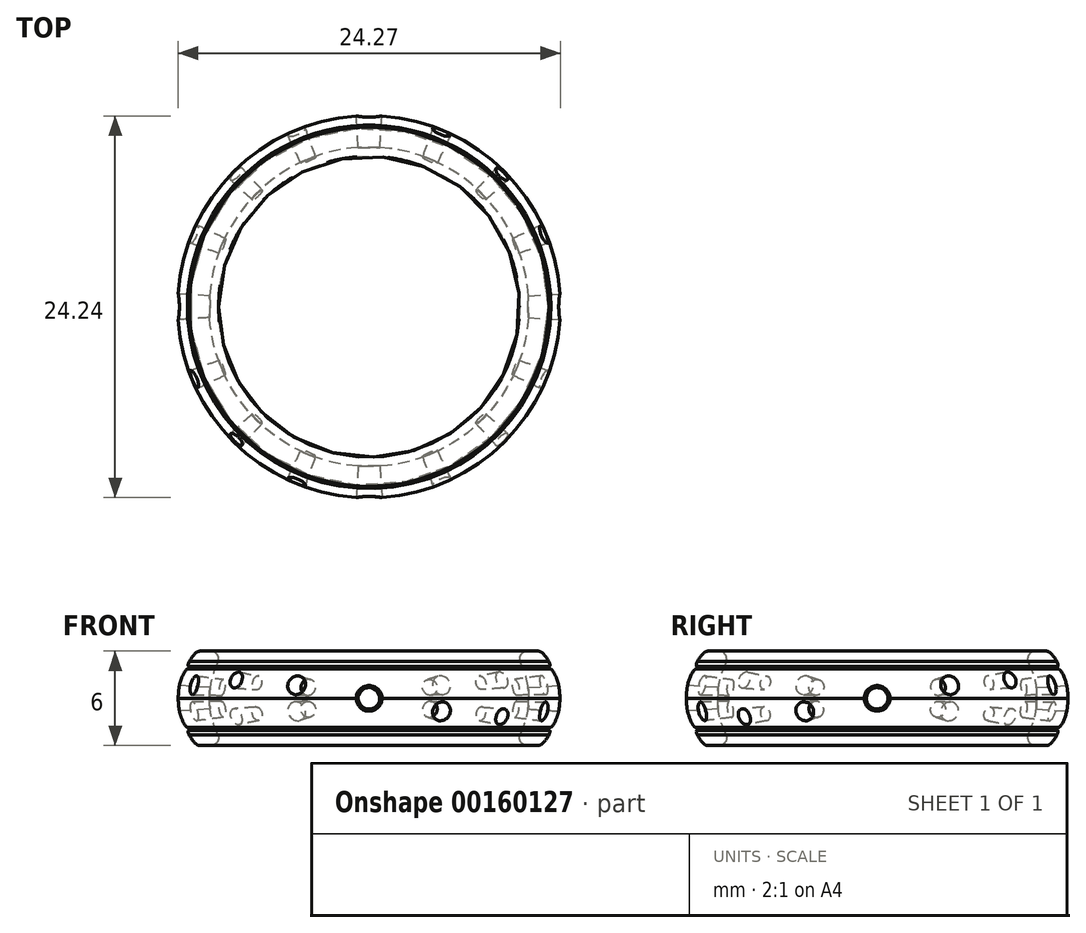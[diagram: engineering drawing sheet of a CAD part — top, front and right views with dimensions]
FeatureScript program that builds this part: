
annotation { "Feature Type Name" : "Feature", "Feature Type Description" : "" }
export const myFeature = defineFeature(function(context is Context, id is Id, definition is map)
    precondition{}
    {
        {
            var Q0;
            Q0=qCreatedBy(makeId("Top.planeOp"),FACE);
            var sketch = newSketch(context, id + "F0", { "sketchPlane" : qUnion([Q0])});
            skCircle(sketch, "E0", {"center": v(0, 0) * mm, "radius": 10.15 * mm});
            skLineSegment(sketch, "E1", {"start": v(-10.15, 0) * mm, "end": v(10.15, 0) * mm, "construction": true});
            skLineSegment(sketch, "E2", {"start": v(0, 10.15) * mm, "end": v(0, -10.15) * mm, "construction": true});
            skCircle(sketch, "E3", {"center": v(0, 0) * mm, "radius": 13.7 * mm});
            skSolve(sketch);
        }
        {
            var Q0;
            Q0=qCreatedBy(makeId("Top.planeOp"),FACE);
            var sketch = newSketch(context, id + "F1", { "sketchPlane" : qUnion([Q0])});
            skCircle(sketch, "E4.0", {"center": v(0, 0) * mm, "radius": 13.7 * mm, "construction": true});
            skLineSegment(sketch, "E5", {"start": v(0, 0) * mm, "end": v(-13.7, 0) * mm, "construction": true});
            skLineSegment(sketch, "E6", {"start": v(-13.7, 4.4) * mm, "end": v(-13.7, -4.4) * mm, "construction": true});
            skLineSegment(sketch, "E7.1.0", {"start": v(0, 0) * mm, "end": v(0, -13.7) * mm, "construction": true});
            skLineSegment(sketch, "E7.1.1", {"start": v(-4.4, -13.7) * mm, "end": v(4.4, -13.7) * mm, "construction": true});
            skLineSegment(sketch, "E7.2.0", {"start": v(0, 0) * mm, "end": v(13.7, 0) * mm, "construction": true});
            skLineSegment(sketch, "E7.2.1", {"start": v(13.7, -4.4) * mm, "end": v(13.7, 4.4) * mm, "construction": true});
            skLineSegment(sketch, "E7.3.0", {"start": v(0, 0) * mm, "end": v(0, 13.7) * mm, "construction": true});
            skLineSegment(sketch, "E7.3.1", {"start": v(4.4, 13.7) * mm, "end": v(-4.4, 13.7) * mm, "construction": true});
            skSolve(sketch);
        }
        {
            var Q0;
            Q0=qCreatedBy(makeId("Top.planeOp"),FACE);
            var sketch = newSketch(context, id + "F2", { "sketchPlane" : qUnion([Q0])});
            skCircle(sketch, "E8.0", {"center": v(0, 0) * mm, "radius": 13.7 * mm});
            skLineSegment(sketch, "E9", {"start": v(0, 0) * mm, "end": v(9.69, -9.69) * mm, "construction": true});
            skLineSegment(sketch, "E10", {"start": v(12.52, -6.86) * mm, "end": v(6.86, -12.52) * mm, "construction": true});
            skLineSegment(sketch, "E11.1.0", {"start": v(6.86, 12.52) * mm, "end": v(12.52, 6.86) * mm, "construction": true});
            skLineSegment(sketch, "E11.1.1", {"start": v(0, 0) * mm, "end": v(9.69, 9.69) * mm, "construction": true});
            skLineSegment(sketch, "E11.2.0", {"start": v(-12.52, 6.86) * mm, "end": v(-6.86, 12.52) * mm, "construction": true});
            skLineSegment(sketch, "E11.2.1", {"start": v(0, 0) * mm, "end": v(-9.69, 9.69) * mm, "construction": true});
            skLineSegment(sketch, "E11.3.0", {"start": v(-6.86, -12.52) * mm, "end": v(-12.52, -6.86) * mm, "construction": true});
            skLineSegment(sketch, "E11.3.1", {"start": v(0, 0) * mm, "end": v(-9.69, -9.69) * mm, "construction": true});
            skSolve(sketch);
        }
        {
            var Q0;
            Q0=qCreatedBy(makeId("Top.planeOp"),FACE);
            var sketch = newSketch(context, id + "F3", { "sketchPlane" : qUnion([Q0])});
            skCircle(sketch, "E12.0", {"center": v(0, 0) * mm, "radius": 13.7 * mm});
            skLineSegment(sketch, "E13", {"start": v(0, 0) * mm, "end": v(5.24, -12.66) * mm, "construction": true});
            skLineSegment(sketch, "E14", {"start": v(3.66, -13.31) * mm, "end": v(6.82, -12) * mm, "construction": true});
            skLineSegment(sketch, "E15.1.0", {"start": v(0, 0) * mm, "end": v(12.66, -5.24) * mm, "construction": true});
            skLineSegment(sketch, "E15.1.1", {"start": v(12, -6.82) * mm, "end": v(13.31, -3.66) * mm, "construction": true});
            skLineSegment(sketch, "E15.2.0", {"start": v(0, 0) * mm, "end": v(12.66, 5.24) * mm, "construction": true});
            skLineSegment(sketch, "E15.2.1", {"start": v(13.31, 3.66) * mm, "end": v(12, 6.82) * mm, "construction": true});
            skLineSegment(sketch, "E15.3.0", {"start": v(0, 0) * mm, "end": v(5.24, 12.66) * mm, "construction": true});
            skLineSegment(sketch, "E15.3.1", {"start": v(6.82, 12) * mm, "end": v(3.66, 13.31) * mm, "construction": true});
            skLineSegment(sketch, "E16.3.4.0", {"start": v(-3.66, 13.31) * mm, "end": v(-6.82, 12) * mm, "construction": true});
            skLineSegment(sketch, "E16.4.4.0", {"start": v(0, 0) * mm, "end": v(-5.24, 12.66) * mm, "construction": true});
            skLineSegment(sketch, "E16.3.5.0", {"start": v(-12, 6.82) * mm, "end": v(-13.31, 3.66) * mm, "construction": true});
            skLineSegment(sketch, "E16.4.5.0", {"start": v(0, 0) * mm, "end": v(-12.66, 5.24) * mm, "construction": true});
            skLineSegment(sketch, "E16.3.6.0", {"start": v(-13.31, -3.66) * mm, "end": v(-12, -6.82) * mm, "construction": true});
            skLineSegment(sketch, "E16.4.6.0", {"start": v(0, 0) * mm, "end": v(-12.66, -5.24) * mm, "construction": true});
            skLineSegment(sketch, "E16.3.7.0", {"start": v(-6.82, -12) * mm, "end": v(-3.66, -13.31) * mm, "construction": true});
            skLineSegment(sketch, "E16.4.7.0", {"start": v(0, 0) * mm, "end": v(-5.24, -12.66) * mm, "construction": true});
            skSolve(sketch);
        }
        {
            var Q0;
            Q0=qCreatedBy(makeId("Front.planeOp"),FACE);
            var sketch = newSketch(context, id + "F4", { "sketchPlane" : qUnion([Q0])});
            skLineSegment(sketch, "E17.0", {"start": v(-10.15, 0) * mm, "end": v(10.15, 0) * mm});
            skLineSegment(sketch, "E18", {"start": v(-10.15, 0) * mm, "end": v(-17.86, 0) * mm, "construction": true});
            skPoint(sketch, "E19", {"position": v(-10.37, 0) * mm});
            skCircle(sketch, "E20", {"center": v(-5.15, 0) * mm, "radius": 5 * mm});
            skFitSpline(sketch, "E21", {"points": [v(-10.37, 3) * mm, v(-11.03, 2.87) * mm, v(-11.53, 2.12) * mm, v(-11.51, 2.04) * mm, v(-11.4, 2.02) * mm, v(-11.4, 1.88) * mm, v(-11.55, 1.85) * mm, v(-12.15, 0) * mm, v(-11.57, -1.84) * mm, v(-11.4, -1.87) * mm, v(-11.38, -2) * mm, v(-11.49, -2.07) * mm, v(-11.11, -2.83) * mm, v(-10.37, -3) * mm], "startDerivative": vector(-13.36, 0) * mm, "endDerivative": vector(14.23, 0) * mm});
            skLineSegment(sketch, "E22", {"start": v(-10.37, 3) * mm, "end": v(-10.15, 3) * mm});
            skLineSegment(sketch, "E23", {"start": v(-9.15, 2) * mm, "end": v(-9.15, -2) * mm});
            skLineSegment(sketch, "E24", {"start": v(-10.15, -3) * mm, "end": v(-10.37, -3) * mm});
            skPoint(sketch, "E25.visualSharp", {"position": v(-9.15, 3) * mm});
            skArc(sketch, "E25.filletArc", {"start": v(-9.15, 2) * mm, "mid": v(-9.44, 2.7) * mm, "end": v(-10.15, 3) * mm});
            skPoint(sketch, "E26.visualSharp", {"position": v(-9.15, -3) * mm});
            skArc(sketch, "E26.filletArc", {"start": v(-10.15, -3) * mm, "mid": v(-9.44, -2.7) * mm, "end": v(-9.15, -2) * mm});
            skLineSegment(sketch, "E27", {"start": v(0, 17.35) * mm, "end": v(0, -28.4) * mm, "construction": true});
            skFitSpline(sketch, "E28.MirrorCS", {"points": [v(-10.37, -3) * mm, v(-11.03, -2.87) * mm, v(-11.53, -2.12) * mm, v(-11.51, -2.04) * mm, v(-11.4, -2.02) * mm, v(-11.4, -1.88) * mm, v(-11.55, -1.85) * mm, v(-12.15, 0) * mm, v(-11.57, 1.84) * mm, v(-11.4, 1.87) * mm, v(-11.38, 2) * mm, v(-11.49, 2.07) * mm, v(-11.11, 2.83) * mm, v(-10.37, 3) * mm], "startDerivative": vector(-13.36, 0) * mm, "endDerivative": vector(14.23, 0) * mm});
            skSolve(sketch);
        }
        {
            var Q0;
            Q0=sQuery(id+"F1.wireOp",EDGE,"E6");
            cPlane(context, id + "F5", {"entities" : qUnion([Q0]), "cplaneType" : CPlaneType.LINE_ANGLE, "offset" : 25 * mm, "angle" : 90 * degree, "width" : 150 * mm, "height" : 150 * mm});
        }
        {
            var Q0;
            Q0=qCreatedBy(id+"F5.planeOp",FACE);
            var sketch = newSketch(context, id + "F6", { "sketchPlane" : qUnion([Q0])});
            skLineSegment(sketch, "E29", {"start": v(0, 2.8) * mm, "end": v(0, -2.73) * mm, "construction": true});
            skCircle(sketch, "E30", {"center": v(0, 0) * mm, "radius": 0.93 * mm});
            skSolve(sketch);
        }
        {
            var Q0;
            Q0=makeQuery(id+"F4.imprint","IMPRINT",FACE,{"disambiguationData":[TD([[makeQuery(id+"F4.imprint","IMPRINT",EDGE,{"derivedFrom":sQuery(id+"F4.wireOp",EDGE,"E21")}),1.0]])]});
            var Q1;
            Q1=sQuery(id+"F4.wireOp",EDGE,"E27");
            revolve(context, id + "F7", {"entities" : qUnion([Q0]), "axis" : qUnion([Q1]), "revolveType" : RevolveType.FULL});
        }
        {
            var Q0;
            Q0=makeQuery(id+"F6.imprint","IMPRINT",FACE,{"disambiguationData":[TD([[makeQuery(id+"F6.imprint","IMPRINT",EDGE,{"derivedFrom":sQuery(id+"F6.wireOp",EDGE,"E30")}),1.0]])]});
            var Q1;
            Q1=sQuery(id+"F1.wireOp",VERTEX,"E4.0.center");
            loft(context, id + "F8", {"operationType" : NewBodyOperationType.REMOVE, "sheetProfilesArray" : [{ "sheetProfileEntities" : qUnion([Q0]) }, { "sheetProfileEntities" : qUnion([Q1]) }]});
        }
        {
            var Q0;
            Q0=sQuery(id+"F1.wireOp",EDGE,"E7.3.1");
            cPlane(context, id + "F9", {"entities" : qUnion([Q0]), "cplaneType" : CPlaneType.LINE_ANGLE, "offset" : 25 * mm, "angle" : 0 * degree, "width" : 150 * mm, "height" : 150 * mm});
        }
        {
            var Q0;
            Q0=qCreatedBy(id+"F9.planeOp",FACE);
            var sketch = newSketch(context, id + "F10", { "sketchPlane" : qUnion([Q0])});
            skCircle(sketch, "E31", {"center": v(0, 0) * mm, "radius": 0.93 * mm});
            skSolve(sketch);
        }
        {
            var Q1;
            Q1=makeQuery(id+"F10.imprint","IMPRINT",FACE,{"disambiguationData":[TD([[makeQuery(id+"F10.imprint","IMPRINT",EDGE,{"derivedFrom":sQuery(id+"F10.wireOp",EDGE,"E31")}),1.0]])]});
            var Q2;
            Q2=sQuery(id+"F1.wireOp",VERTEX,"E4.0.center");
            loft(context, id + "F11", {"operationType" : NewBodyOperationType.REMOVE, "sheetProfilesArray" : [{ "sheetProfileEntities" : qUnion([Q1]) }, { "sheetProfileEntities" : qUnion([Q2]) }]});
        }
        {
            var Q0;
            Q0=sQuery(id+"F1.wireOp",EDGE,"E7.2.1");
            cPlane(context, id + "F12", {"entities" : qUnion([Q0]), "cplaneType" : CPlaneType.LINE_ANGLE, "offset" : 25 * mm, "angle" : 90 * degree, "width" : 150 * mm, "height" : 150 * mm});
        }
        {
            var Q0;
            Q0=qCreatedBy(id+"F12.planeOp",FACE);
            var sketch = newSketch(context, id + "F13", { "sketchPlane" : qUnion([Q0])});
            skCircle(sketch, "E32", {"center": v(0, 0) * mm, "radius": 0.93 * mm});
            skSolve(sketch);
        }
        {
            var Q1;
            Q1=makeQuery(id+"F13.imprint","IMPRINT",FACE,{"disambiguationData":[TD([[makeQuery(id+"F13.imprint","IMPRINT",EDGE,{"derivedFrom":sQuery(id+"F13.wireOp",EDGE,"E32")}),1.0]])]});
            var Q2;
            Q2=sQuery(id+"F1.wireOp",VERTEX,"E4.0.center");
            loft(context, id + "F14", {"operationType" : NewBodyOperationType.REMOVE, "sheetProfilesArray" : [{ "sheetProfileEntities" : qUnion([Q1]) }, { "sheetProfileEntities" : qUnion([Q2]) }]});
        }
        {
            var Q0;
            Q0=sQuery(id+"F1.wireOp",EDGE,"E7.1.1");
            cPlane(context, id + "F15", {"entities" : qUnion([Q0]), "cplaneType" : CPlaneType.LINE_ANGLE, "offset" : 25 * mm, "angle" : 0 * degree, "width" : 150 * mm, "height" : 150 * mm});
        }
        {
            var Q0;
            Q0=qCreatedBy(id+"F15.planeOp",FACE);
            var sketch = newSketch(context, id + "F16", { "sketchPlane" : qUnion([Q0])});
            skCircle(sketch, "E33", {"center": v(0, 0) * mm, "radius": 0.93 * mm});
            skSolve(sketch);
        }
        {
            var Q1;
            Q1=makeQuery(id+"F16.imprint","IMPRINT",FACE,{"disambiguationData":[TD([[makeQuery(id+"F16.imprint","IMPRINT",EDGE,{"derivedFrom":sQuery(id+"F16.wireOp",EDGE,"E33")}),1.0]])]});
            var Q2;
            Q2=sQuery(id+"F1.wireOp",VERTEX,"E4.0.center");
            loft(context, id + "F17", {"operationType" : NewBodyOperationType.REMOVE, "sheetProfilesArray" : [{ "sheetProfileEntities" : qUnion([Q1]) }, { "sheetProfileEntities" : qUnion([Q2]) }]});
        }
        {
            var Q0;
            Q0=sQuery(id+"F2.wireOp",EDGE,"E10");
            cPlane(context, id + "F18", {"entities" : qUnion([Q0]), "cplaneType" : CPlaneType.LINE_ANGLE, "offset" : 25 * mm, "angle" : 90 * degree, "width" : 150 * mm, "height" : 150 * mm});
        }
        {
            var Q0;
            Q0=qCreatedBy(id+"F18.planeOp",FACE);
            var sketch = newSketch(context, id + "F19", { "sketchPlane" : qUnion([Q0])});
            skLineSegment(sketch, "E34", {"start": v(0, 0) * mm, "end": v(0, -6.97) * mm, "construction": true});
            skCircle(sketch, "E35", {"center": v(0, -1.35) * mm, "radius": 0.6 * mm});
            skSolve(sketch);
        }
        {
            var Q1;
            Q1=makeQuery(id+"F19.imprint","IMPRINT",FACE,{"disambiguationData":[TD([[makeQuery(id+"F19.imprint","IMPRINT",EDGE,{"derivedFrom":sQuery(id+"F19.wireOp",EDGE,"E35")}),1.0]])]});
            var Q2;
            Q2=sQuery(id+"F1.wireOp",VERTEX,"E4.0.center");
            loft(context, id + "F20", {"operationType" : NewBodyOperationType.REMOVE, "sheetProfilesArray" : [{ "sheetProfileEntities" : qUnion([Q1]) }, { "sheetProfileEntities" : qUnion([Q2]) }]});
        }
        {
            var Q0;
            Q0=sQuery(id+"F2.wireOp",EDGE,"E11.3.0");
            cPlane(context, id + "F21", {"entities" : qUnion([Q0]), "cplaneType" : CPlaneType.LINE_ANGLE, "offset" : 25 * mm, "angle" : 90 * degree, "width" : 150 * mm, "height" : 150 * mm});
        }
        {
            var Q0;
            Q0=qCreatedBy(id+"F21.planeOp",FACE);
            var sketch = newSketch(context, id + "F22", { "sketchPlane" : qUnion([Q0])});
            skLineSegment(sketch, "E36", {"start": v(0, -4.31) * mm, "end": v(0, 5.75) * mm, "construction": true});
            skCircle(sketch, "E37", {"center": v(0, 1.35) * mm, "radius": 0.6 * mm});
            skSolve(sketch);
        }
        {
            var Q1;
            Q1=makeQuery(id+"F22.imprint","IMPRINT",FACE,{"disambiguationData":[TD([[makeQuery(id+"F22.imprint","IMPRINT",EDGE,{"derivedFrom":sQuery(id+"F22.wireOp",EDGE,"E37")}),1.0]])]});
            var Q2;
            Q2=sQuery(id+"F1.wireOp",VERTEX,"E4.0.center");
            loft(context, id + "F23", {"operationType" : NewBodyOperationType.REMOVE, "sheetProfilesArray" : [{ "sheetProfileEntities" : qUnion([Q1]) }, { "sheetProfileEntities" : qUnion([Q2]) }]});
        }
        {
            var Q0;
            Q0=sQuery(id+"F2.wireOp",EDGE,"E11.2.0");
            cPlane(context, id + "F24", {"entities" : qUnion([Q0]), "cplaneType" : CPlaneType.LINE_ANGLE, "offset" : 25 * mm, "angle" : 90 * degree, "width" : 150 * mm, "height" : 150 * mm});
        }
        {
            var Q0;
            Q0=qCreatedBy(id+"F24.planeOp",FACE);
            var sketch = newSketch(context, id + "F25", { "sketchPlane" : qUnion([Q0])});
            skLineSegment(sketch, "E38", {"start": v(0, 5.18) * mm, "end": v(0, -5.52) * mm, "construction": true});
            skCircle(sketch, "E39", {"center": v(0, -1.35) * mm, "radius": 0.6 * mm});
            skSolve(sketch);
        }
        {
            var Q1;
            Q1=makeQuery(id+"F25.imprint","IMPRINT",FACE,{"disambiguationData":[TD([[makeQuery(id+"F25.imprint","IMPRINT",EDGE,{"derivedFrom":sQuery(id+"F25.wireOp",EDGE,"E39")}),1.0]])]});
            var Q2;
            Q2=sQuery(id+"F1.wireOp",VERTEX,"E4.0.center");
            loft(context, id + "F26", {"operationType" : NewBodyOperationType.REMOVE, "sheetProfilesArray" : [{ "sheetProfileEntities" : qUnion([Q1]) }, { "sheetProfileEntities" : qUnion([Q2]) }]});
        }
        {
            var Q0;
            Q0=sQuery(id+"F2.wireOp",EDGE,"E11.1.0");
            cPlane(context, id + "F27", {"entities" : qUnion([Q0]), "cplaneType" : CPlaneType.LINE_ANGLE, "offset" : 25 * mm, "angle" : 90 * degree, "width" : 150 * mm, "height" : 150 * mm});
        }
        {
            var Q0;
            Q0=qCreatedBy(id+"F27.planeOp",FACE);
            var sketch = newSketch(context, id + "F28", { "sketchPlane" : qUnion([Q0])});
            skLineSegment(sketch, "E40", {"start": v(0, -3.41) * mm, "end": v(0, 4.01) * mm, "construction": true});
            skCircle(sketch, "E41", {"center": v(0, 1.35) * mm, "radius": 0.6 * mm});
            skSolve(sketch);
        }
        {
            var Q1;
            Q1=makeQuery(id+"F28.imprint","IMPRINT",FACE,{"disambiguationData":[TD([[makeQuery(id+"F28.imprint","IMPRINT",EDGE,{"derivedFrom":sQuery(id+"F28.wireOp",EDGE,"E41")}),1.0]])]});
            var Q2;
            Q2=sQuery(id+"F1.wireOp",VERTEX,"E4.0.center");
            loft(context, id + "F29", {"operationType" : NewBodyOperationType.REMOVE, "sheetProfilesArray" : [{ "sheetProfileEntities" : qUnion([Q1]) }, { "sheetProfileEntities" : qUnion([Q2]) }]});
        }
        {
            var Q0;
            Q0=sQuery(id+"F3.wireOp",EDGE,"E14");
            cPlane(context, id + "F30", {"entities" : qUnion([Q0]), "cplaneType" : CPlaneType.LINE_ANGLE, "offset" : 25 * mm, "angle" : 0 * degree, "width" : 150 * mm, "height" : 150 * mm});
        }
        {
            var Q0;
            Q0=qCreatedBy(id+"F30.planeOp",FACE);
            var sketch = newSketch(context, id + "F31", { "sketchPlane" : qUnion([Q0])});
            skLineSegment(sketch, "E42", {"start": v(0, 1.86) * mm, "end": v(0, -3.93) * mm, "construction": true});
            skCircle(sketch, "E43", {"center": v(0, -0.95) * mm, "radius": 0.7 * mm});
            skSolve(sketch);
        }
        {
            var Q1;
            Q1=makeQuery(id+"F31.imprint","IMPRINT",FACE,{"disambiguationData":[TD([[makeQuery(id+"F31.imprint","IMPRINT",EDGE,{"derivedFrom":sQuery(id+"F31.wireOp",EDGE,"E43")}),1.0]])]});
            var Q2;
            Q2=sQuery(id+"F3.wireOp",VERTEX,"E12.0.center");
            loft(context, id + "F32", {"operationType" : NewBodyOperationType.REMOVE, "sheetProfilesArray" : [{ "sheetProfileEntities" : qUnion([Q1]) }, { "sheetProfileEntities" : qUnion([Q2]) }]});
        }
        {
            var Q0;
            Q0=sQuery(id+"F3.wireOp",EDGE,"E16.3.7.0");
            cPlane(context, id + "F33", {"entities" : qUnion([Q0]), "cplaneType" : CPlaneType.LINE_ANGLE, "offset" : 25 * mm, "angle" : 0 * degree, "width" : 150 * mm, "height" : 150 * mm});
        }
        {
            var Q0;
            Q0=qCreatedBy(id+"F33.planeOp",FACE);
            var sketch = newSketch(context, id + "F34", { "sketchPlane" : qUnion([Q0])});
            skLineSegment(sketch, "E44", {"start": v(0, -5.3) * mm, "end": v(0, 5.97) * mm, "construction": true});
            skCircle(sketch, "E45", {"center": v(0, 0.95) * mm, "radius": 0.7 * mm});
            skSolve(sketch);
        }
        {
            var Q1;
            Q1=makeQuery(id+"F34.imprint","IMPRINT",FACE,{"disambiguationData":[TD([[makeQuery(id+"F34.imprint","IMPRINT",EDGE,{"derivedFrom":sQuery(id+"F34.wireOp",EDGE,"E45")}),1.0]])]});
            var Q2;
            Q2=sQuery(id+"F3.wireOp",VERTEX,"E12.0.center");
            loft(context, id + "F35", {"operationType" : NewBodyOperationType.REMOVE, "sheetProfilesArray" : [{ "sheetProfileEntities" : qUnion([Q1]) }, { "sheetProfileEntities" : qUnion([Q2]) }]});
        }
        {
            var Q0;
            Q0=sQuery(id+"F3.wireOp",EDGE,"E16.3.6.0");
            cPlane(context, id + "F36", {"entities" : qUnion([Q0]), "cplaneType" : CPlaneType.LINE_ANGLE, "offset" : 25 * mm, "angle" : 90 * degree, "width" : 150 * mm, "height" : 150 * mm});
        }
        {
            var Q0;
            Q0=qCreatedBy(id+"F36.planeOp",FACE);
            var sketch = newSketch(context, id + "F37", { "sketchPlane" : qUnion([Q0])});
            skLineSegment(sketch, "E46", {"start": v(0, -0.9) * mm, "end": v(0, 3) * mm, "construction": true});
            skCircle(sketch, "E47", {"center": v(0, 0.95) * mm, "radius": 0.7 * mm});
            skSolve(sketch);
        }
        {
            var Q1;
            Q1=makeQuery(id+"F37.imprint","IMPRINT",FACE,{"disambiguationData":[TD([[makeQuery(id+"F37.imprint","IMPRINT",EDGE,{"derivedFrom":sQuery(id+"F37.wireOp",EDGE,"E47")}),1.0]])]});
            var Q2;
            Q2=sQuery(id+"F3.wireOp",VERTEX,"E12.0.center");
            loft(context, id + "F38", {"operationType" : NewBodyOperationType.REMOVE, "sheetProfilesArray" : [{ "sheetProfileEntities" : qUnion([Q1]) }, { "sheetProfileEntities" : qUnion([Q2]) }]});
        }
        {
            var Q0;
            Q0=sQuery(id+"F3.wireOp",EDGE,"E16.3.5.0");
            cPlane(context, id + "F39", {"entities" : qUnion([Q0]), "cplaneType" : CPlaneType.LINE_ANGLE, "offset" : 25 * mm, "angle" : 90 * degree, "width" : 150 * mm, "height" : 150 * mm});
        }
        {
            var Q0;
            Q0=qCreatedBy(id+"F39.planeOp",FACE);
            var sketch = newSketch(context, id + "F40", { "sketchPlane" : qUnion([Q0])});
            skLineSegment(sketch, "E48", {"start": v(0, 0) * mm, "end": v(0, -1.9) * mm, "construction": true});
            skCircle(sketch, "E49", {"center": v(0, -0.95) * mm, "radius": 0.7 * mm});
            skSolve(sketch);
        }
        {
            var Q1;
            Q1=makeQuery(id+"F40.imprint","IMPRINT",FACE,{"disambiguationData":[TD([[makeQuery(id+"F40.imprint","IMPRINT",EDGE,{"derivedFrom":sQuery(id+"F40.wireOp",EDGE,"E49")}),1.0]])]});
            var Q2;
            Q2=sQuery(id+"F3.wireOp",VERTEX,"E12.0.center");
            loft(context, id + "F41", {"operationType" : NewBodyOperationType.REMOVE, "sheetProfilesArray" : [{ "sheetProfileEntities" : qUnion([Q1]) }, { "sheetProfileEntities" : qUnion([Q2]) }]});
        }
        {
            var Q0;
            Q0=sQuery(id+"F3.wireOp",EDGE,"E16.3.4.0");
            cPlane(context, id + "F42", {"entities" : qUnion([Q0]), "cplaneType" : CPlaneType.LINE_ANGLE, "offset" : 25 * mm, "angle" : 0 * degree, "width" : 150 * mm, "height" : 150 * mm});
        }
        {
            var Q0;
            Q0=qCreatedBy(id+"F42.planeOp",FACE);
            var sketch = newSketch(context, id + "F43", { "sketchPlane" : qUnion([Q0])});
            skLineSegment(sketch, "E50", {"start": v(0, 0) * mm, "end": v(0, -3.77) * mm, "construction": true});
            skCircle(sketch, "E51", {"center": v(0, -0.95) * mm, "radius": 0.7 * mm});
            skSolve(sketch);
        }
        {
            var Q1;
            Q1=sQuery(id+"F3.wireOp",VERTEX,"E12.0.center");
            var Q2;
            Q2=makeQuery(id+"F43.imprint","IMPRINT",FACE,{"disambiguationData":[TD([[makeQuery(id+"F43.imprint","IMPRINT",EDGE,{"derivedFrom":sQuery(id+"F43.wireOp",EDGE,"E51")}),1.0]])]});
            loft(context, id + "F44", {"operationType" : NewBodyOperationType.REMOVE, "sheetProfilesArray" : [{ "sheetProfileEntities" : qUnion([Q1]) }, { "sheetProfileEntities" : qUnion([Q2]) }]});
        }
        {
            var Q0;
            Q0=sQuery(id+"F3.wireOp",EDGE,"E15.3.1");
            cPlane(context, id + "F45", {"entities" : qUnion([Q0]), "cplaneType" : CPlaneType.LINE_ANGLE, "offset" : 25 * mm, "angle" : 0 * degree, "width" : 150 * mm, "height" : 150 * mm});
        }
        {
            var Q0;
            Q0=qCreatedBy(id+"F45.planeOp",FACE);
            var sketch = newSketch(context, id + "F46", { "sketchPlane" : qUnion([Q0])});
            skLineSegment(sketch, "E52", {"start": v(0, 0) * mm, "end": v(0, 2.17) * mm, "construction": true});
            skCircle(sketch, "E53", {"center": v(0, 0.95) * mm, "radius": 0.7 * mm});
            skSolve(sketch);
        }
        {
            var Q1;
            Q1=makeQuery(id+"F46.imprint","IMPRINT",FACE,{"disambiguationData":[TD([[makeQuery(id+"F46.imprint","IMPRINT",EDGE,{"derivedFrom":sQuery(id+"F46.wireOp",EDGE,"E53")}),1.0]])]});
            var Q2;
            Q2=sQuery(id+"F3.wireOp",VERTEX,"E12.0.center");
            loft(context, id + "F47", {"operationType" : NewBodyOperationType.REMOVE, "sheetProfilesArray" : [{ "sheetProfileEntities" : qUnion([Q1]) }, { "sheetProfileEntities" : qUnion([Q2]) }]});
        }
        {
            var Q0;
            Q0=sQuery(id+"F3.wireOp",EDGE,"E15.2.1");
            cPlane(context, id + "F48", {"entities" : qUnion([Q0]), "cplaneType" : CPlaneType.LINE_ANGLE, "offset" : 25 * mm, "angle" : 90 * degree, "width" : 150 * mm, "height" : 150 * mm});
        }
        {
            var Q0;
            Q0=qCreatedBy(id+"F48.planeOp",FACE);
            var sketch = newSketch(context, id + "F49", { "sketchPlane" : qUnion([Q0])});
            skLineSegment(sketch, "E54", {"start": v(0, 0) * mm, "end": v(0, 3.06) * mm, "construction": true});
            skCircle(sketch, "E55", {"center": v(0, 0.95) * mm, "radius": 0.7 * mm});
            skSolve(sketch);
        }
        {
            var Q1;
            Q1=makeQuery(id+"F49.imprint","IMPRINT",FACE,{"disambiguationData":[TD([[makeQuery(id+"F49.imprint","IMPRINT",EDGE,{"derivedFrom":sQuery(id+"F49.wireOp",EDGE,"E55")}),1.0]])]});
            var Q2;
            Q2=sQuery(id+"F3.wireOp",VERTEX,"E12.0.center");
            loft(context, id + "F50", {"operationType" : NewBodyOperationType.REMOVE, "sheetProfilesArray" : [{ "sheetProfileEntities" : qUnion([Q1]) }, { "sheetProfileEntities" : qUnion([Q2]) }]});
        }
        {
            var Q0;
            Q0=sQuery(id+"F3.wireOp",EDGE,"E15.1.1");
            cPlane(context, id + "F51", {"entities" : qUnion([Q0]), "cplaneType" : CPlaneType.LINE_ANGLE, "offset" : 25 * mm, "angle" : 90 * degree, "width" : 150 * mm, "height" : 150 * mm});
        }
        {
            var Q0;
            Q0=qCreatedBy(id+"F51.planeOp",FACE);
            var sketch = newSketch(context, id + "F52", { "sketchPlane" : qUnion([Q0])});
            skLineSegment(sketch, "E56", {"start": v(0, 0) * mm, "end": v(0, -1.7) * mm, "construction": true});
            skCircle(sketch, "E57", {"center": v(0, -0.95) * mm, "radius": 0.7 * mm});
            skSolve(sketch);
        }
        {
            var Q1;
            Q1=makeQuery(id+"F52.imprint","IMPRINT",FACE,{"disambiguationData":[TD([[makeQuery(id+"F52.imprint","IMPRINT",EDGE,{"derivedFrom":sQuery(id+"F52.wireOp",EDGE,"E57")}),1.0]])]});
            var Q2;
            Q2=sQuery(id+"F3.wireOp",VERTEX,"E12.0.center");
            loft(context, id + "F53", {"operationType" : NewBodyOperationType.REMOVE, "sheetProfilesArray" : [{ "sheetProfileEntities" : qUnion([Q1]) }, { "sheetProfileEntities" : qUnion([Q2]) }]});
        }
        {
            var Q0;
            Q0=makeQuery(id+"F7.opRevolve","SWEPT_EDGE",EDGE,{"disambiguationData":[OSD([sQuery(id+"F4.wireOp",EDGE,"E20"),sQuery(id+"F4.wireOp",EDGE,"E25.filletArc")])]});
            var Q1;
            Q1=makeQuery(id+"F7.opRevolve","SWEPT_EDGE",EDGE,{"disambiguationData":[OSD([sQuery(id+"F4.wireOp",EDGE,"E20"),sQuery(id+"F4.wireOp",EDGE,"E26.filletArc")])]});
            fillet(context, id + "F54", {"entities" : qUnion([Q0, Q1]), "radius" : .5 * mm, "tangentPropagation" : true, "allowEdgeOverflow" : false});
        }
    });
